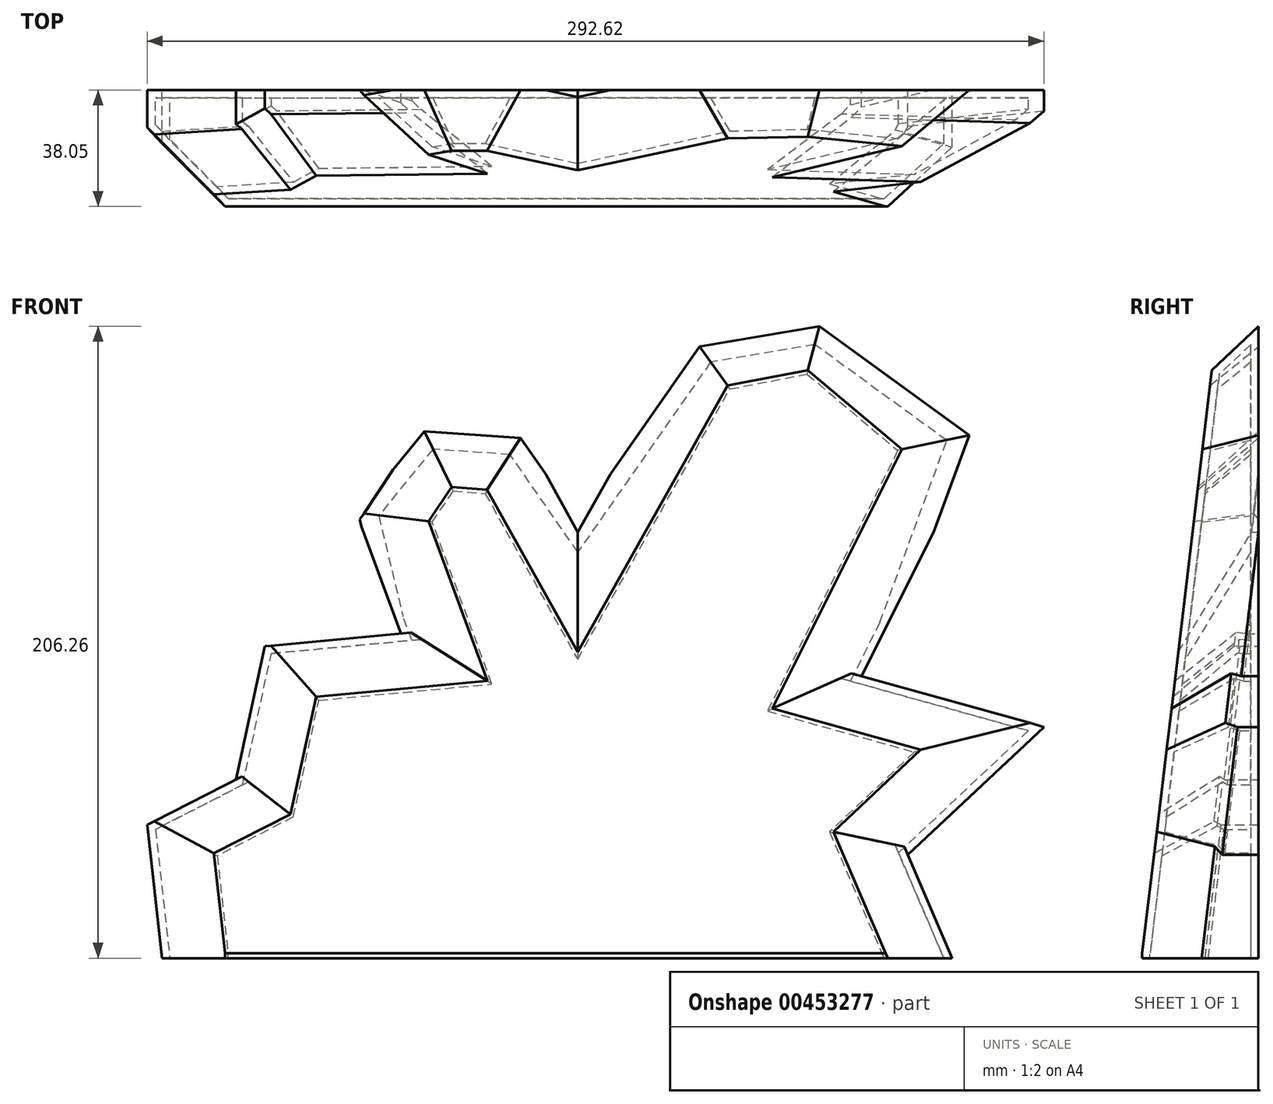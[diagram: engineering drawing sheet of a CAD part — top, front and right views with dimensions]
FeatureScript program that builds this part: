
annotation { "Feature Type Name" : "Feature", "Feature Type Description" : "" }
export const myFeature = defineFeature(function(context is Context, id is Id, definition is map)
    precondition{}
    {
        {
            var Q0;
            Q0=qCreatedBy(makeId("Front.planeOp"),FACE);
            var sketch = newSketch(context, id + "F0", { "sketchPlane" : qUnion([Q0])});
            skLineSegment(sketch, "E0", {"start": v(174.12, -12) * mm, "end": v(183.6, 31.5) * mm});
            skLineSegment(sketch, "E1", {"start": v(183.6, 31.5) * mm, "end": v(227.97, 35.64) * mm});
            skLineSegment(sketch, "E2", {"start": v(227.97, 35.64) * mm, "end": v(214.36, 72.63) * mm});
            skLineSegment(sketch, "E3", {"start": v(214.36, 72.63) * mm, "end": v(234.19, 102.21) * mm});
            skLineSegment(sketch, "E4", {"start": v(174.12, -12) * mm, "end": v(145.13, -26.79) * mm});
            skLineSegment(sketch, "E5", {"start": v(145.13, -26.79) * mm, "end": v(149.98, -70.28) * mm});
            skLineSegment(sketch, "E6", {"start": v(149.98, -70.28) * mm, "end": v(407.86, -70.28) * mm});
            skLineSegment(sketch, "E7", {"start": v(234.19, 102.21) * mm, "end": v(268.5, 99.55) * mm});
            skLineSegment(sketch, "E8", {"start": v(268.5, 99.55) * mm, "end": v(285.67, 68.78) * mm});
            skLineSegment(sketch, "E9", {"start": v(285.67, 68.78) * mm, "end": v(321.47, 132.4) * mm});
            skLineSegment(sketch, "E10", {"start": v(321.47, 132.4) * mm, "end": v(366.44, 140.97) * mm});
            skLineSegment(sketch, "E11", {"start": v(366.44, 140.97) * mm, "end": v(416.74, 98.66) * mm});
            skLineSegment(sketch, "E12", {"start": v(416.74, 98.66) * mm, "end": v(378.28, 21.74) * mm});
            skLineSegment(sketch, "E13", {"start": v(378.28, 21.74) * mm, "end": v(437.75, 5.17) * mm});
            skLineSegment(sketch, "E14", {"start": v(437.75, 5.17) * mm, "end": v(393.37, -36.55) * mm});
            skLineSegment(sketch, "E15", {"start": v(393.37, -36.55) * mm, "end": v(407.86, -70.28) * mm});
            skSolve(sketch);
        }
        {
            var Q0;
            Q0=makeQuery(id+"F0.imprint","IMPRINT",FACE,{"disambiguationData":[TD([[makeQuery(id+"F0.imprint","IMPRINT",EDGE,{"derivedFrom":sQuery(id+"F0.wireOp",EDGE,"E0")}),-1.0]])]});
            extrude(context, id + "F1", {"entities" : qUnion([Q0]), "depth" : 38.1 * mm});
        }
        {
            var Q0;
            Q0=qCreatedBy(makeId("Right.planeOp"),FACE);
            cPlane(context, id + "F2", {"entities" : qUnion([Q0]), "cplaneType" : CPlaneType.OFFSET, "offset" : 76.2 * mm, "oppositeDirection" : true, "width" : 152.4 * mm, "height" : 152.4 * mm});
        }
        {
            var Q0;
            Q0=qCreatedBy(id+"F2.planeOp",FACE);
            var sketch = newSketch(context, id + "F3", { "sketchPlane" : qUnion([Q0])});
            skLineSegment(sketch, "E16", {"start": v(-38.19, -70.6) * mm, "end": v(0, 248.97) * mm});
            skLineSegment(sketch, "E17", {"start": v(0, 248.97) * mm, "end": v(-45.77, 254.44) * mm});
            skLineSegment(sketch, "E18", {"start": v(-45.77, 254.44) * mm, "end": v(-38.19, -70.6) * mm});
            skSolve(sketch);
        }
        {
            var Q0;
            Q0=qSketchRegion(id+"F3",true);
            extrude(context, id + "F4", {"entities" : qUnion([Q0]), "operationType" : NewBodyOperationType.REMOVE, "endBound" : BoundingType.THROUGH_ALL, "depth" : 25.4 * mm});
        }
        {
            var Q0;
            Q0=makeQuery(id+"F4.boolean.opBoolean","COPY",FACE,{"derivedFrom":makeQuery(id+"F4.opExtrude","SWEPT_FACE",FACE,{"disambiguationData":[OSD([sQuery(id+"F3.wireOp",EDGE,"E16")])]})});
            chamfer(context, id + "F5", {"entities" : qUnion([Q0]), "width" : 20.32 * mm, "tangentPropagation" : true});
        }
        {
            var Q0;
            Q0=makeQuery(id+"F1.opExtrude","SWEPT_FACE",FACE,{"disambiguationData":[OSD([sQuery(id+"F0.wireOp",EDGE,"5UBScBti-lYJG-QWJU-C9wr-LBJ0cxTIyK4E")])]});
            var Q1;
            Q1=makeQuery(id+"F1.opExtrude","SWEPT_FACE",FACE,{"disambiguationData":[OSD([sQuery(id+"F0.wireOp",EDGE,"E6")])]});
            shell(context, id + "F6", {"entities" : qUnion([Q0, Q1]), "thickness" : 2.54 * mm});
        }
    });
